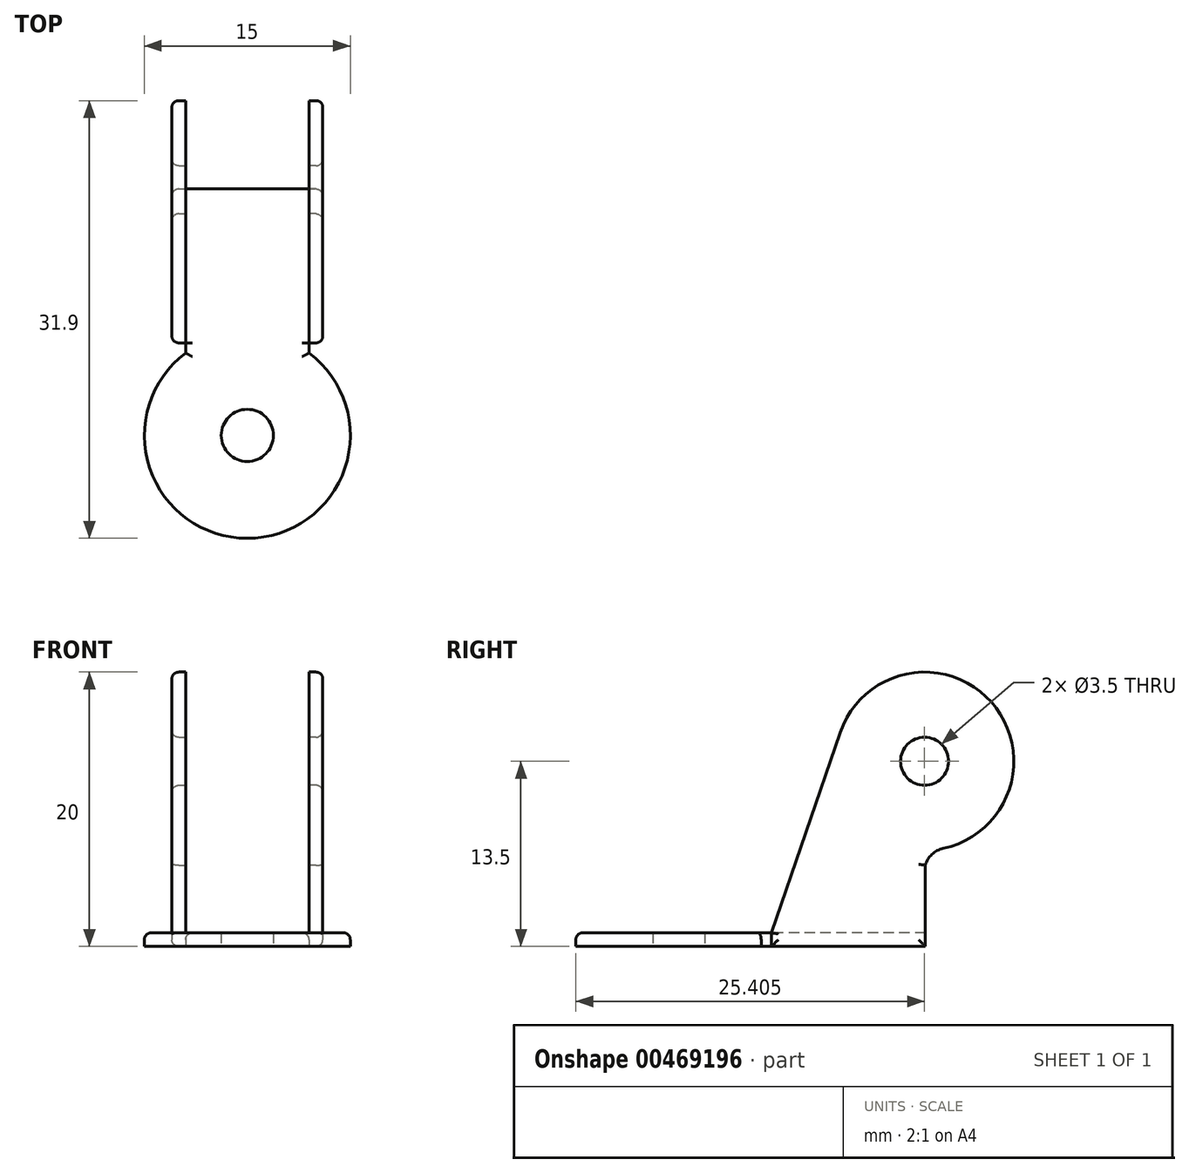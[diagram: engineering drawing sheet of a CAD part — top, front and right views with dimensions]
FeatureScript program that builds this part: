
annotation { "Feature Type Name" : "Feature", "Feature Type Description" : "" }
export const myFeature = defineFeature(function(context is Context, id is Id, definition is map)
    precondition{}
    {
        {
            var Q0;
            Q0=qCreatedBy(makeId("Top.planeOp"),FACE);
            var sketch = newSketch(context, id + "F0", { "sketchPlane" : qUnion([Q0])});
            skCircle(sketch, "E0", {"center": v(0, 0) * mm, "radius": 7.5 * mm});
            skLineSegment(sketch, "E1.bottom", {"start": v(-4.5, 17.96) * mm, "end": v(4.5, 17.96) * mm});
            skLineSegment(sketch, "E1.top", {"start": v(-4.5, 6) * mm, "end": v(4.5, 6) * mm});
            skLineSegment(sketch, "E1.left", {"start": v(-4.5, 17.96) * mm, "end": v(-4.5, 6) * mm});
            skLineSegment(sketch, "E1.right", {"start": v(4.5, 17.96) * mm, "end": v(4.5, 6) * mm});
            skPoint(sketch, "E2", {"position": v(0, 6) * mm});
            skCircle(sketch, "E3", {"center": v(0, 0) * mm, "radius": 1.9 * mm});
            skSolve(sketch);
        }
        {
            var Q0;
            Q0 = qSketchRegion(id + "F0", true);
            extrude(context, id + "F1", {"entities" : qUnion([Q0]), "depth" : 1 * mm});
        }
        {
            var Q0;
            Q0=makeQuery(id+"F1.opExtrude","SWEPT_FACE",FACE,{"disambiguationData":[OSD([sQuery(id+"F0.wireOp",EDGE,"E1.right")])]});
            var sketch = newSketch(context, id + "F2", { "sketchPlane" : qUnion([Q0])});
            skLineSegment(sketch, "E4", {"start": v(6.74, 1) * mm, "end": v(11.76, 15.6) * mm});
            skArc(sketch, "E5", {"start": v(11.76, 15.6) * mm, "mid": v(22.77, 17.81) * mm, "end": v(19.26, 7.14) * mm});
            skArc(sketch, "E6", {"start": v(19.26, 7.14) * mm, "mid": v(18.45, 6.71) * mm, "end": v(17.96, 5.92) * mm});
            skLineSegment(sketch, "E7", {"start": v(17.96, 5.92) * mm, "end": v(17.96, 0) * mm});
            skLineSegment(sketch, "E8", {"start": v(6.74, 1) * mm, "end": v(6.74, 0) * mm});
            skLineSegment(sketch, "E9", {"start": v(6.74, 0) * mm, "end": v(17.96, 0) * mm});
            skCircle(sketch, "E10", {"center": v(17.9, 13.5) * mm, "radius": 1.75 * mm});
            skSolve(sketch);
        }
        {
            var Q0;
            Q0 = qSketchRegion(id + "F2", true);
            extrude(context, id + "F3", {"entities" : qUnion([Q0]), "operationType" : NewBodyOperationType.ADD, "depth" : 1 * mm});
        }
        {
            var Q0;
            Q0=makeQuery(id+"F3.opExtrude","CAP_FACE",FACE,{"disambiguationData":[OSD([sQuery(id+"F2.wireOp",EDGE,"E4"),sQuery(id+"F2.wireOp",EDGE,"E5"),sQuery(id+"F2.wireOp",EDGE,"E6"),sQuery(id+"F2.wireOp",EDGE,"E7"),sQuery(id+"F2.wireOp",EDGE,"E8"),sQuery(id+"F2.wireOp",EDGE,"E9"),sQuery(id+"F2.wireOp",EDGE,"E10")])],"isStart":false});
            fillet(context, id + "F4", {"entities" : qUnion([Q0]), "radius" : .5 * mm, "tangentPropagation" : true, "allowEdgeOverflow" : false});
        }
        {
            var Q0;
            Q0=makeQuery(id+"F1.opExtrude","SWEPT_BODY",BODY,{"disambiguationData":[OSD([sQuery(id+"F0.wireOp",EDGE,"E0"),sQuery(id+"F0.wireOp",EDGE,"E1.bottom"),sQuery(id+"F0.wireOp",EDGE,"E1.left"),sQuery(id+"F0.wireOp",EDGE,"E1.right"),sQuery(id+"F0.wireOp",EDGE,"E3")])]});
            var Q1;
            Q1=qCreatedBy(makeId("Right.planeOp"),FACE);
            mirror(context, id + "F5", {"operationType" : NewBodyOperationType.ADD, "entities" : qUnion([Q0]), "mirrorPlane" : qUnion([Q1])});
        }
        {
            var Q0;
            Q0=makeQuery(id+"F1.opExtrude","CAP_EDGE",EDGE,{"disambiguationData":[OSD([sQuery(id+"F0.wireOp",EDGE,"E0")])],"isStart":false});
            var Q1;
            Q1=makeQuery(id+"F5.boolean.opBoolean","SPLIT",EDGE,{"derivedFrom":makeQuery(id+"F1.opExtrude","CAP_EDGE",EDGE,{"disambiguationData":[OSD([sQuery(id+"F0.wireOp",EDGE,"E1.left")])],"isStart":false})});
            var Q2;
            {var subQ0=sQuery(id+"F0.wireOp",EDGE,"E1.right");Q2=makeQuery(id+"F3.boolean.opBoolean","SPLIT",EDGE,{"disambiguationData":[topologyDisambiguationEdgeConnected([makeQuery(id+"F1.opExtrude","SWEPT_FACE",FACE,{"disambiguationData":[OSD([subQ0])]})])],"derivedFrom":makeQuery(id+"F1.opExtrude","CAP_EDGE",EDGE,{"disambiguationData":[OSD([subQ0])],"isStart":false})});}
            fillet(context, id + "F6", {"entities" : qUnion([Q0, Q1, Q2]), "radius" : .5 * mm, "tangentPropagation" : true, "allowEdgeOverflow" : false});
        }
    });
